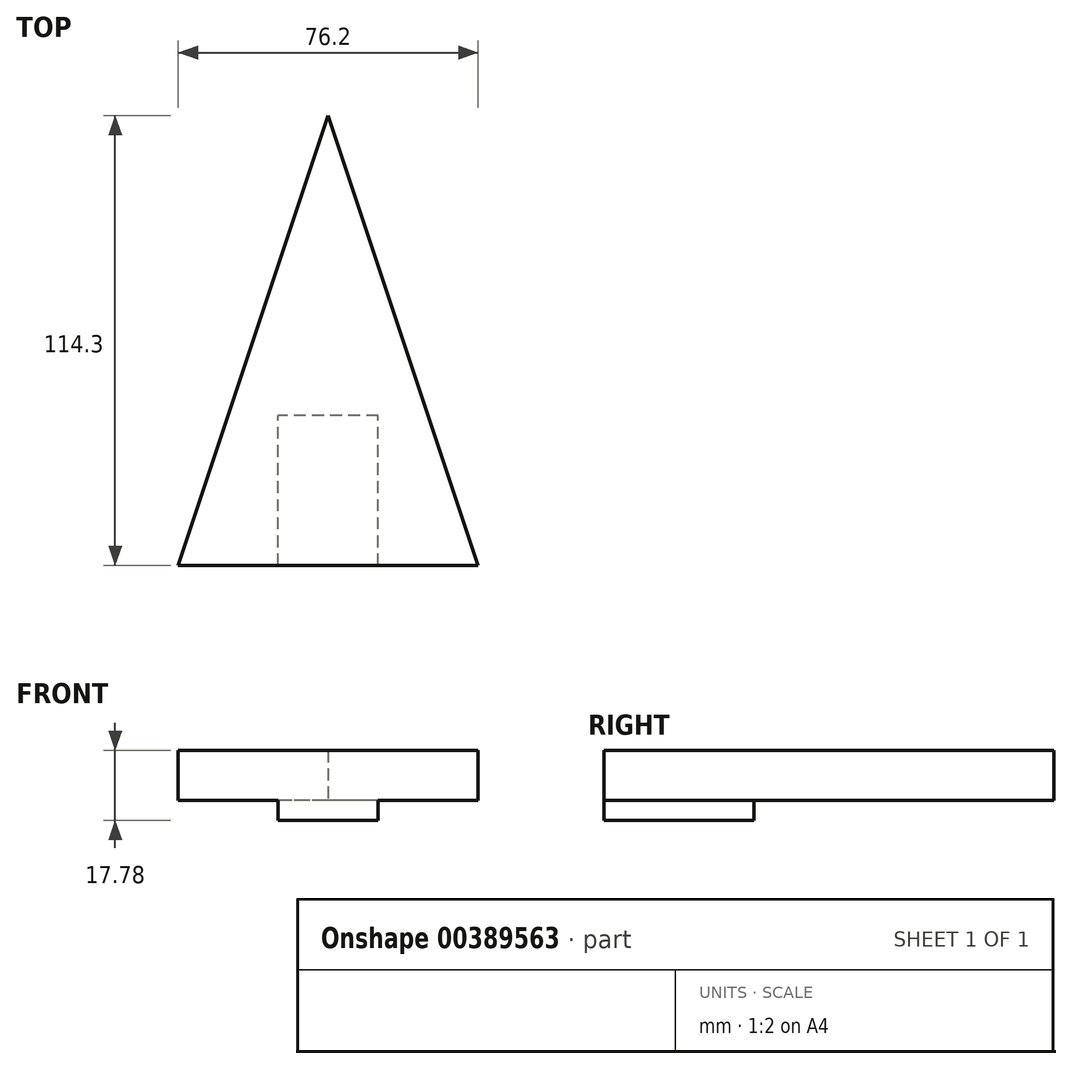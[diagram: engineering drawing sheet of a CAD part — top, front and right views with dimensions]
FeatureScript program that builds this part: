
annotation { "Feature Type Name" : "Feature", "Feature Type Description" : "" }
export const myFeature = defineFeature(function(context is Context, id is Id, definition is map)
    precondition{}
    {
        {
            var Q0;
            Q0=qCreatedBy(makeId("Top.planeOp"),FACE);
            var sketch = newSketch(context, id + "F0", { "sketchPlane" : qUnion([Q0])});
            skLineSegment(sketch, "E0", {"start": v(-38.1, -38.1) * mm, "end": v(38.1, -38.1) * mm});
            skLineSegment(sketch, "E1", {"start": v(38.1, -38.1) * mm, "end": v(0, 76.2) * mm});
            skLineSegment(sketch, "E2", {"start": v(0, 76.2) * mm, "end": v(-38.1, -38.1) * mm});
            skSolve(sketch);
        }
        {
            var Q0;
            Q0=makeQuery(id+"F0.imprint","IMPRINT",FACE,{"disambiguationData":[TD([[makeQuery(id+"F0.imprint","IMPRINT",EDGE,{"derivedFrom":sQuery(id+"F0.wireOp",EDGE,"E0")}),1.0]])]});
            extrude(context, id + "F1", {"entities" : qUnion([Q0]), "depth" : 12.7 * mm});
        }
        {
            var Q0;
            Q0=makeQuery(id+"F1.opExtrude","CAP_FACE",FACE,{"disambiguationData":[OSD([sQuery(id+"F0.wireOp",EDGE,"E0"),sQuery(id+"F0.wireOp",EDGE,"E1"),sQuery(id+"F0.wireOp",EDGE,"E2")])],"isStart":true});
            var sketch = newSketch(context, id + "F2", { "sketchPlane" : qUnion([Q0])});
            skLineSegment(sketch, "E3.bottom", {"start": v(12.7, 38.1) * mm, "end": v(-12.7, 38.1) * mm});
            skLineSegment(sketch, "E3.top", {"start": v(12.7, 0) * mm, "end": v(-12.7, 0) * mm});
            skLineSegment(sketch, "E3.left", {"start": v(12.7, 38.1) * mm, "end": v(12.7, 0) * mm});
            skLineSegment(sketch, "E3.right", {"start": v(-12.7, 38.1) * mm, "end": v(-12.7, 0) * mm});
            skSolve(sketch);
        }
        {
            var Q0;
            Q0=makeQuery(id+"F2.imprint","IMPRINT",FACE,{"disambiguationData":[TD([[makeQuery(id+"F2.imprint","IMPRINT",EDGE,{"derivedFrom":sQuery(id+"F2.wireOp",EDGE,"E3.bottom")}),-1.0]])]});
            extrude(context, id + "F3", {"entities" : qUnion([Q0]), "operationType" : NewBodyOperationType.ADD, "depth" : 5.08 * mm});
        }
    });
